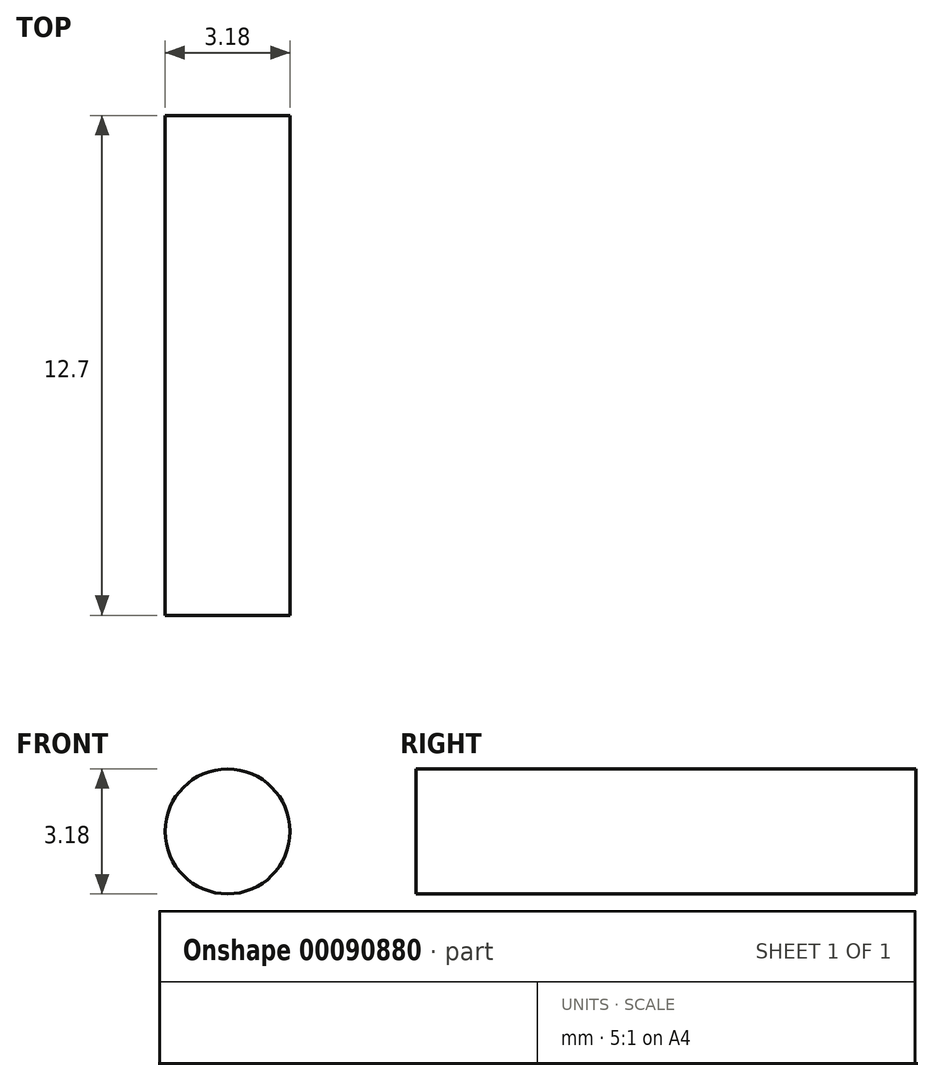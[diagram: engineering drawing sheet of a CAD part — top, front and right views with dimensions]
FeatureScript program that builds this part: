
annotation { "Feature Type Name" : "Feature", "Feature Type Description" : "" }
export const myFeature = defineFeature(function(context is Context, id is Id, definition is map)
    precondition{}
    {
        {
            var Q0;
            Q0=qCreatedBy(makeId("Front.planeOp"),FACE);
            var sketch = newSketch(context, id + "F0", { "sketchPlane" : qUnion([Q0])});
            skCircle(sketch, "E0", {"center": v(0, 0) * mm, "radius": 1.59 * mm});
            skSolve(sketch);
        }
        {
            var Q0;
            Q0 = qSketchRegion(id + "F0", true);
            extrude(context, id + "F1", {"entities" : qUnion([Q0]), "endBound" : BoundingType.SYMMETRIC, "depth" : 12.7 * mm});
        }
    });
